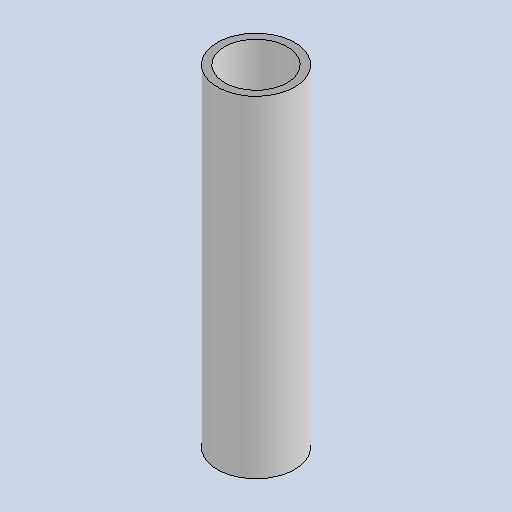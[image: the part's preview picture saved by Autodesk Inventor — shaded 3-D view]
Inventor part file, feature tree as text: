
AUTODESK INVENTOR PART (.ipt)
format: ipt  version: 2025.1 (Build 291241020, 241B)  size: 118,272 bytes
history: native  units: mm
features: extrude x1, sketch x1
ambient origin geometry x8: Origin, YZ Plane, XZ Plane, XY Plane, X Axis, Y Axis, Z Axis, Center Point
bodies: Body1 (feature_tree)
feature tree (2):
  extrude  "Extrusion5"  Depth=90.0mm
  sketch  "Sketch11"  dims[d187=21.0mm d188=2.0mm d189=90.0mm d190=0.0mm]
